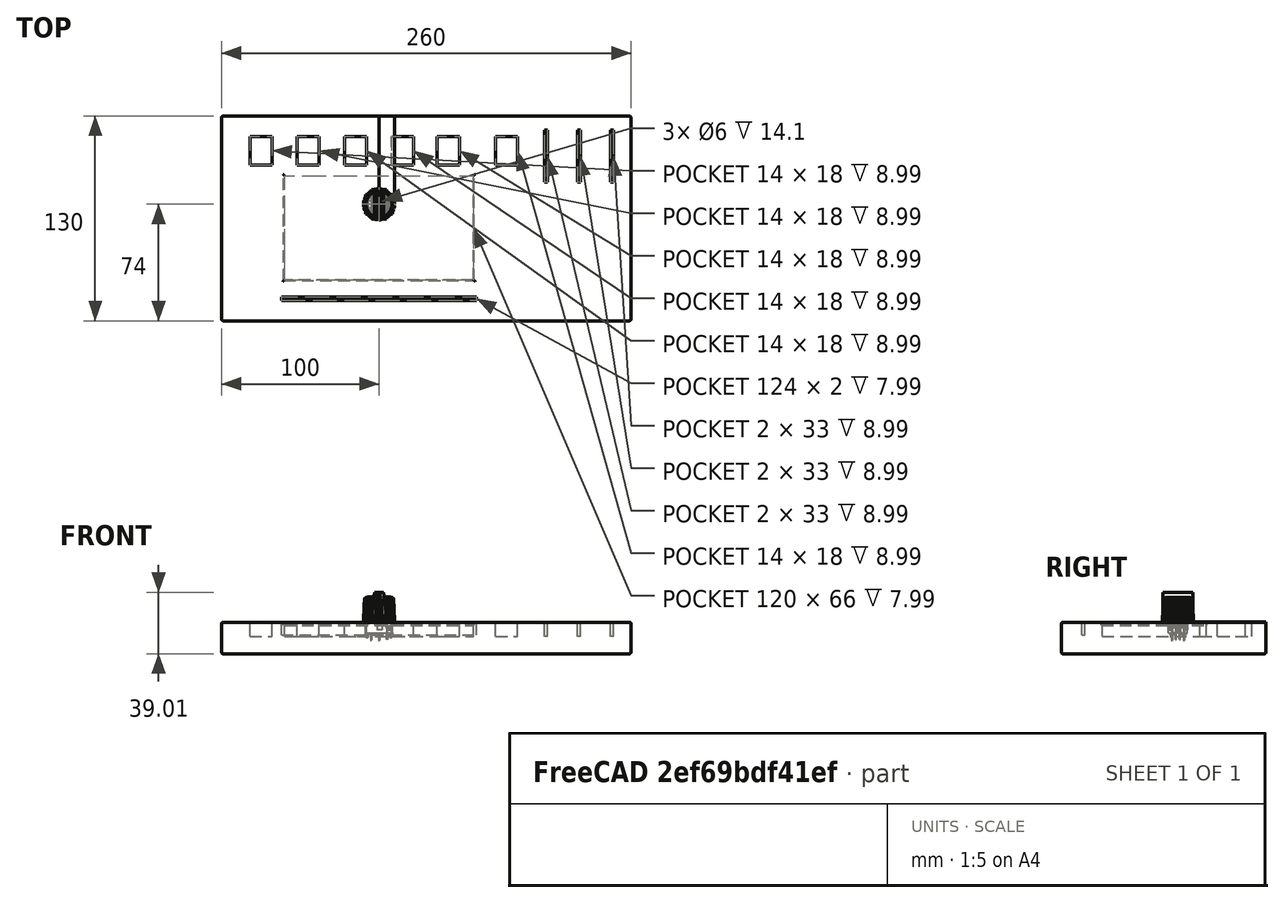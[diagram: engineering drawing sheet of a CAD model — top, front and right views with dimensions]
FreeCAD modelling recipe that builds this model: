
FCSTD DOCUMENT  (FreeCAD 0.18R14220 (Git))
Label: draw-toy
License: All rights reserved
LicenseURL: http://en.wikipedia.org/wiki/All_rights_reserved
objects: Part::Feature×42, Part::Box×33, App::DocumentObjectGroupPython×28, App::Part×20, Part::Cone×3, Part::Fillet×2, Part::Cut×2, Part::MultiFuse×1
note: 83 computed .brp shape members not serialized (recipe doc carries the construction recipe); baked Part::Feature solids carry a one-line shape summary decoded from their .brp

FEATURE [Part::Feature] Pocket004001  label="CrossfaderTop001"
  Placement = pos=(0,0,0) rot=(1,0,0;1.5708rad)
  shape: bbox 9.6 x 19 x 15 mm, 18 faces (baked)
FEATURE [Part::Feature] Pad001001  label="CrossfaderNeck001"
  Placement = pos=(0,0,0) rot=(1,0,0;1.5708rad)
  shape: bbox 6 x 1.2 x 12 mm, 12 faces (baked)
FEATURE [Part::Feature] Pocket004039  label="CrossfaderTop002"
  Placement = pos=(0,0,0) rot=(1,0,0;1.5708rad)
  shape: bbox 9.6 x 19 x 15 mm, 18 faces (baked)
FEATURE [Part::Feature] Pad001011  label="CrossfaderNeck002"
  Placement = pos=(0,0,0) rot=(1,0,0;1.5708rad)
  shape: bbox 6 x 1.2 x 12 mm, 12 faces (baked)
FEATURE [Part::Feature] Pad001012  label="CrossfaderNeck003"
  Placement = pos=(0,0,0) rot=(1,0,0;1.5708rad)
  shape: bbox 6 x 1.2 x 12 mm, 12 faces (baked)
FEATURE [Part::Feature] Pocket004040  label="CrossfaderTop003"
  Placement = pos=(0,0,0) rot=(1,0,0;1.5708rad)
  shape: bbox 9.6 x 19 x 15 mm, 18 faces (baked)
FEATURE [Part::Feature] Pad001013  label="CrossfaderNeck004"
  Placement = pos=(0,0,0) rot=(1,0,0;1.5708rad)
  shape: bbox 6 x 1.2 x 12 mm, 12 faces (baked)
FEATURE [Part::Feature] Pocket004041  label="CrossfaderTop004"
  Placement = pos=(0,0,0) rot=(1,0,0;1.5708rad)
  shape: bbox 9.6 x 19 x 15 mm, 18 faces (baked)
FEATURE [Part::Box] Box  label="Cube"
  AttacherType = Attacher::AttachEngine3D
  Height = 20
  Length = 260
  Placement = pos=(-100,-74,-20.01) rot=(0,0,1;0rad)
  Width = 130
FEATURE [Part::Fillet] Fillet004
  Base = -> Box
  Edges = 12 edges r=1: [Edge1,Edge2,Edge3,Edge4,Edge5,Edge6,Edge7,Edge8,Edge9,Edge10,Edge11,Edge12]
FEATURE [Part::Box] Box001  label="CF-Eraser-Hole"
  AttacherType = Attacher::AttachEngine3D
  Height = 10
  Length = 124
  Placement = pos=(-62,-61,-8) rot=(0,0,1;0rad)
  Width = 2
FEATURE [Part::Box] Box002  label="Btn4-Hole"
  AttacherType = Attacher::AttachEngine3D
  Height = 10
  Length = 14
  Placement = pos=(8,25,-9) rot=(0,0,1;0rad)
  Width = 18
FEATURE [Part::Box] Box003  label="Btn3-Hole"
  AttacherType = Attacher::AttachEngine3D
  Height = 10
  Length = 14
  Placement = pos=(-22,25,-9) rot=(0,0,1;0rad)
  Width = 18
FEATURE [Part::Box] Box004  label="Btn2-Hole"
  AttacherType = Attacher::AttachEngine3D
  Height = 10
  Length = 14
  Placement = pos=(-52,25,-9) rot=(0,0,1;0rad)
  Width = 18
FEATURE [Part::Box] Box005  label="Btn1-Hole"
  AttacherType = Attacher::AttachEngine3D
  Height = 10
  Length = 14
  Placement = pos=(-82,25,-9) rot=(0,0,1;0rad)
  Width = 18
FEATURE [Part::Box] Box006  label="CF-Red-Hole"
  AttacherType = Attacher::AttachEngine3D
  Height = 10
  Length = 33
  Placement = pos=(107,14,-9) rot=(0,0,1;1.5708rad)
  Width = 2
FEATURE [Part::Box] Box009  label="CF-Green-Hole"
  AttacherType = Attacher::AttachEngine3D
  Height = 10
  Length = 33
  Placement = pos=(128,14,-9) rot=(0,0,1;1.5708rad)
  Width = 2
FEATURE [Part::Box] Box010  label="CF-Blue-Hole"
  AttacherType = Attacher::AttachEngine3D
  Height = 10
  Length = 33
  Placement = pos=(149,14,-9) rot=(0,0,1;1.5708rad)
  Width = 2
FEATURE [Part::Feature] Pocket001  label="Knob002"
  Placement = pos=(0,0,0) rot=(0,0,-1;4.99164rad)
  shape: bbox 19.76 x 19.76 x 16.1 mm, 124 faces (baked)
FEATURE [Part::Feature] Pocket004042  label="Knob003"
  Placement = pos=(0,0,0) rot=(0,0,-1;2.61799rad)
  shape: bbox 19.73 x 19.73 x 16.1 mm, 124 faces (baked)
FEATURE [Part::Feature] Pocket004043  label="Knob004"
  Placement = pos=(0,0,0) rot=(0,0,-1;0.349066rad)
  shape: bbox 19.8 x 19.8 x 16.1 mm, 124 faces (baked)
FEATURE [Part::Feature] Pocket004044  label="Rot4"
  Placement = pos=(0,0,0) rot=(0,0,-1;5.41052rad)
  shape: bbox 19.8 x 19.8 x 16.1 mm, 124 faces (baked)
FEATURE [Part::Feature] Compound002  label="DigitastPins001"
  shape: bbox 16.24 x 8.62 x 4.5 mm, 46 faces, 8 solids (baked)
FEATURE [Part::Feature] Pocket006001  label="DigitastBase001"
  shape: bbox 17.3 x 12.3 x 7.9 mm, 98 faces (baked)
FEATURE [Part::Feature] Revolution001  label="ObjMode1Led"
  Placement = pos=(5.12923,-0.028118,-0.1) rot=(0.57735,0.57735,0.57735;2.0944rad)
  shape: bbox 3.4 x 3.4 x 4.5 mm, 5 faces (baked)
FEATURE [Part::Feature] Cylinder001
  Placement = pos=(7,-5,-3) rot=(-1,0,0;1.5708rad)
  shape: bbox 0.8 x 10 x 0.8 mm, 3 faces (baked)
FEATURE [Part::Feature] Pocket010001  label="DigitastTop001"
  Placement = pos=(0,0,0) rot=(1,0,0;1.5708rad)
  shape: bbox 17.1 x 12.3 x 10.94 mm, 34 faces (baked)
FEATURE [Part::Feature] Compound003  label="DigitastPins002"
  shape: bbox 16.24 x 8.62 x 4.5 mm, 46 faces, 8 solids (baked)
FEATURE [Part::Feature] Pocket010002  label="DigitastBase002"
  shape: bbox 17.3 x 12.3 x 7.9 mm, 98 faces (baked)
FEATURE [Part::Feature] Cylinder002
  Placement = pos=(7,-5,-3) rot=(-1,0,0;1.5708rad)
  shape: bbox 0.8 x 10 x 0.8 mm, 3 faces (baked)
FEATURE [Part::Feature] Revolution002  label="ObjMode2Led"
  Placement = pos=(5.12923,-0.028118,-0.1) rot=(0.57735,0.57735,0.57735;2.0944rad)
  shape: bbox 3.4 x 3.4 x 4.5 mm, 5 faces (baked)
FEATURE [Part::Feature] Pocket010003  label="DigitastTop002"
  Placement = pos=(0,0,0) rot=(1,0,0;1.5708rad)
  shape: bbox 17.1 x 12.3 x 10.94 mm, 34 faces (baked)
FEATURE [Part::Feature] Compound004  label="DigitastPins003"
  shape: bbox 16.24 x 8.62 x 4.5 mm, 46 faces, 8 solids (baked)
FEATURE [Part::Feature] Pocket010004  label="DigitastBase003"
  shape: bbox 17.3 x 12.3 x 7.9 mm, 98 faces (baked)
FEATURE [Part::Feature] Cylinder003
  Placement = pos=(7,-5,-3) rot=(-1,0,0;1.5708rad)
  shape: bbox 0.8 x 10 x 0.8 mm, 3 faces (baked)
FEATURE [Part::Feature] Revolution003  label="ObjMode3Led"
  Placement = pos=(5.12923,-0.028118,-0.1) rot=(0.57735,0.57735,0.57735;2.0944rad)
  shape: bbox 3.4 x 3.4 x 4.5 mm, 5 faces (baked)
FEATURE [Part::Feature] Pocket010005  label="DigitastTop003"
  Placement = pos=(0,0,0) rot=(1,0,0;1.5708rad)
  shape: bbox 17.1 x 12.3 x 10.94 mm, 34 faces (baked)
FEATURE [Part::Feature] Compound005  label="DigitastPins004"
  shape: bbox 16.24 x 8.62 x 4.5 mm, 46 faces, 8 solids (baked)
FEATURE [Part::Feature] Pocket010006  label="DigitastBase004"
  shape: bbox 17.3 x 12.3 x 7.9 mm, 98 faces (baked)
FEATURE [Part::Feature] Cylinder004
  Placement = pos=(7,-5,-3) rot=(-1,0,0;1.5708rad)
  shape: bbox 0.8 x 10 x 0.8 mm, 3 faces (baked)
FEATURE [Part::Feature] Revolution004  label="ObjMode4Led"
  Placement = pos=(5.12923,-0.028118,-0.1) rot=(0.57735,0.57735,0.57735;2.0944rad)
  shape: bbox 3.4 x 3.4 x 4.5 mm, 5 faces (baked)
FEATURE [Part::Feature] Pocket010007  label="DigitastTop004"
  Placement = pos=(0,0,0) rot=(1,0,0;1.5708rad)
  shape: bbox 17.1 x 12.3 x 10.94 mm, 34 faces (baked)
FEATURE [Part::Box] Box011  label="DisplayBackground"
  AttacherType = Attacher::AttachEngine3D
  Height = 1
  Length = 121
  Placement = pos=(-60.5,-48.5,-2) rot=(0,0,1;0rad)
  Width = 67
FEATURE [Part::Box] Box012  label="Cube002"
  AttacherType = Attacher::AttachEngine3D
  Height = 0.01
  Length = 121
  Placement = pos=(-60.5,-48.5,-1) rot=(0,0,1;0rad)
  Width = 67
FEATURE [App::DocumentObjectGroupPython] FPSimDisplay  # scripted group (container) (typed FeaturePython)
  Group = -> [Box012]
  ResolutionX = 300
  ResolutionY = 200
FEATURE [Part::Box] Box013  label="Cube003"
  AttacherType = Attacher::AttachEngine3D
  Height = 10
  Length = 120
  Placement = pos=(-60,-48,-9) rot=(0,0,1;0rad)
  Width = 66
FEATURE [App::DocumentObjectGroupPython] FPSimButton  label="Mode1Btn"  # scripted group (container) (typed FeaturePython)
  Group = -> [Pocket010001,Cylinder001]
  RotationAngle = -6
  RotationAxis = (0,1,0)
  RotationCenter = (7,5,-3)
  SwitchMode = false
  Translation = (0.3,0,0)
FEATURE [App::DocumentObjectGroupPython] FPSimButton001  label="Mode2Btn"  # scripted group (container) (typed FeaturePython)
  Group = -> [Pocket010003,Cylinder002]
  RotationAngle = -6
  RotationAxis = (0,1,0)
  RotationCenter = (7,5,-3)
  SwitchMode = false
  Translation = (0.3,0,0)
FEATURE [App::DocumentObjectGroupPython] FPSimButton002  label="Mode3Btn"  # scripted group (container) (typed FeaturePython)
  Group = -> [Pocket010005,Cylinder003]
  RotationAngle = -6
  RotationAxis = (0,1,0)
  RotationCenter = (7,5,-3)
  SwitchMode = false
  Translation = (0.3,0,0)
FEATURE [App::DocumentObjectGroupPython] FPSimButton003  label="Mode4Btn"  # scripted group (container) (typed FeaturePython)
  Group = -> [Pocket010007,Cylinder004]
  RotationAngle = -6
  RotationAxis = (0,1,0)
  RotationCenter = (7,5,-3)
  SwitchMode = false
  Translation = (0.3,0,0)
FEATURE [Part::Box] Box014  label="Cube004"
  AttacherType = Attacher::AttachEngine3D
  Height = 0.01
  Length = 121
  Placement = pos=(-60.5,-48.5,-0.9) rot=(0,0,1;0rad)
  Width = 67
FEATURE [Part::Feature] Compound006  label="DigitastPins005"
  shape: bbox 16.24 x 8.62 x 4.5 mm, 46 faces, 8 solids (baked)
FEATURE [Part::Feature] Pocket010008  label="DigitastBase005"
  shape: bbox 17.3 x 12.3 x 7.9 mm, 98 faces (baked)
FEATURE [Part::Feature] Revolution005  label="ObjColorModLed"
  Placement = pos=(5.12923,-0.028118,-0.1) rot=(0.57735,0.57735,0.57735;2.0944rad)
  shape: bbox 3.4 x 3.4 x 4.5 mm, 5 faces (baked)
FEATURE [Part::Feature] Cylinder005
  Placement = pos=(7,-5,-3) rot=(-1,0,0;1.5708rad)
  shape: bbox 0.8 x 10 x 0.8 mm, 3 faces (baked)
FEATURE [Part::Feature] Pocket010009  label="DigitastTop005"
  Placement = pos=(0,0,0) rot=(1,0,0;1.5708rad)
  shape: bbox 17.1 x 12.3 x 10.94 mm, 34 faces (baked)
FEATURE [App::DocumentObjectGroupPython] FPSimButton004  label="ColorAutomationBtn"  # scripted group (container) (typed FeaturePython)
  Group = -> [Pocket010009,Cylinder005]
  RotationAngle = -6
  RotationAxis = (0,1,0)
  RotationCenter = (7,5,-3)
  SwitchMode = false
  Translation = (0.3,0,0)
FEATURE [Part::Box] Box015  label="ModBtnHole"
  AttacherType = Attacher::AttachEngine3D
  Height = 10
  Length = 14
  Placement = pos=(74,25,-9) rot=(0,0,1;0rad)
  Width = 18
FEATURE [App::DocumentObjectGroupPython] FPSimRotaryEncoder  label="X_POS1"  # scripted group (container) (typed FeaturePython)
  Group = -> [Pocket001]
  IncrementsPerRev = 64
  MouseSensitivity = 1
  NumSnapInPositions = 0
  PushButton = false
  PushButtonDepth = 1
  RotationAxis = (0,0,-1)
  RotationCenter = (0,0,0)
FEATURE [App::Part] Part  label="Rot001"
  Group = -> [Pocket001,FPSimRotaryEncoder]
  License = CC BY 3.0
  LicenseURL = http://creativecommons.org/licenses/by/3.0/
  Origin = -> Origin
  Placement = pos=(-79,0,1) rot=(0,0,1;0rad)
FEATURE [App::DocumentObjectGroupPython] FPSimRotaryEncoder001  label="Y_POS1"  # scripted group (container) (typed FeaturePython)
  Group = -> [Pocket004042]
  IncrementsPerRev = 64
  MouseSensitivity = 1
  NumSnapInPositions = 0
  PushButton = false
  PushButtonDepth = 1
  RotationAxis = (0,0,-1)
  RotationCenter = (0,0,0)
FEATURE [App::Part] Part012  label="Rot002"
  Group = -> [Pocket004042,FPSimRotaryEncoder001]
  License = CC BY 3.0
  LicenseURL = http://creativecommons.org/licenses/by/3.0/
  Origin = -> Origin013
  Placement = pos=(-79,-37,1) rot=(0,0,1;0rad)
FEATURE [App::DocumentObjectGroupPython] FPSimRotaryEncoder002  label="X_POS2"  # scripted group (container) (typed FeaturePython)
  Group = -> [Pocket004043]
  IncrementsPerRev = 64
  MouseSensitivity = 1
  NumSnapInPositions = 0
  PushButton = false
  PushButtonDepth = 1
  RotationAxis = (0,0,-1)
  RotationCenter = (0,0,0)
FEATURE [App::Part] Part014  label="Rot004"
  Group = -> [Pocket004043,FPSimRotaryEncoder002]
  License = CC BY 3.0
  LicenseURL = http://creativecommons.org/licenses/by/3.0/
  Origin = -> Origin015
  Placement = pos=(80,0,1) rot=(0,0,1;0rad)
FEATURE [App::DocumentObjectGroupPython] FPSimRotaryEncoder003  label="Y_POS2"  # scripted group (container) (typed FeaturePython)
  Group = -> [Pocket004044]
  IncrementsPerRev = 64
  MouseSensitivity = 1
  NumSnapInPositions = 0
  PushButton = false
  PushButtonDepth = 1
  RotationAxis = (0,0,-1)
  RotationCenter = (0,0,0)
FEATURE [App::Part] Part013  label="Rot003"
  Group = -> [Pocket004044,FPSimRotaryEncoder003]
  License = CC BY 3.0
  LicenseURL = http://creativecommons.org/licenses/by/3.0/
  Origin = -> Origin014
  Placement = pos=(80,-37,1) rot=(0,0,1;0rad)
FEATURE [Part::Cone] Cone
  Angle = 360
  AttacherType = Attacher::AttachEngine3D
  Height = 10
  Placement = pos=(0,0,10) rot=(1,0,0;3.14159rad)
  Radius1 = 4
  Radius2 = 5
FEATURE [Part::Box] Box016  label="Cube005"
  AttacherType = Attacher::AttachEngine3D
  Height = 10
  Length = 1
  Placement = pos=(-0.5,0,0) rot=(0,0,1;0rad)
  Width = 5
FEATURE [Part::Cone] Cone001
  Angle = 360
  AttacherType = Attacher::AttachEngine3D
  Height = 10
  Placement = pos=(0,0,10) rot=(1,0,0;3.14159rad)
  Radius1 = 4
  Radius2 = 5
FEATURE [Part::Box] Box017  label="Cube006"
  AttacherType = Attacher::AttachEngine3D
  Height = 10
  Length = 1
  Placement = pos=(-0.5,0,0) rot=(0,0,1;0rad)
  Width = 5
FEATURE [Part::Cone] Cone002
  Angle = 360
  AttacherType = Attacher::AttachEngine3D
  Height = 10
  Placement = pos=(0,0,10) rot=(1,0,0;3.14159rad)
  Radius1 = 4
  Radius2 = 5
FEATURE [Part::Box] Box018  label="Cube007"
  AttacherType = Attacher::AttachEngine3D
  Height = 10
  Length = 1
  Placement = pos=(-0.5,0,0) rot=(0,0,1;0rad)
  Width = 5
FEATURE [App::DocumentObjectGroupPython] FPSimRotaryPotentiometer  label="PotFreqRed"  # scripted group (container) (typed FeaturePython)
  Group = -> [Box016,Cone]
  IncrementsOnWholeArc = 64
  MouseSensitivity = 1
  NegativeRotLimitDeg = 120
  NumSnapInPositions = 0
  PositiveRotLimitDeg = 120
  RotationAxis = (0,0,-1)
  RotationCenter = (0,0,0)
FEATURE [App::Part] Part020  label="PartFreqRed"
  Group = -> [Cone,Box016,FPSimRotaryPotentiometer]
  License = CC BY 3.0
  LicenseURL = http://creativecommons.org/licenses/by/3.0/
  Origin = -> Origin021
  Placement = pos=(106,0,0) rot=(0,0,1;0rad)
FEATURE [App::DocumentObjectGroupPython] FPSimRotaryPotentiometer001  label="PotFreqGreen"  # scripted group (container) (typed FeaturePython)
  Group = -> [Box017,Cone001]
  IncrementsOnWholeArc = 64
  MouseSensitivity = 1
  NegativeRotLimitDeg = 120
  NumSnapInPositions = 0
  PositiveRotLimitDeg = 120
  RotationAxis = (0,0,-1)
  RotationCenter = (0,0,0)
FEATURE [App::Part] Part021  label="PartFreqGreen"
  Group = -> [Cone001,Box017,FPSimRotaryPotentiometer001]
  License = CC BY 3.0
  LicenseURL = http://creativecommons.org/licenses/by/3.0/
  Origin = -> Origin022
  Placement = pos=(127,0,0) rot=(0,0,1;0rad)
FEATURE [App::DocumentObjectGroupPython] FPSimRotaryPotentiometer002  label="PotFreqBlue"  # scripted group (container) (typed FeaturePython)
  Group = -> [Box018,Cone002]
  IncrementsOnWholeArc = 64
  MouseSensitivity = 1
  NegativeRotLimitDeg = 120
  NumSnapInPositions = 0
  PositiveRotLimitDeg = 120
  RotationAxis = (0,0,-1)
  RotationCenter = (0,0,0)
FEATURE [App::Part] Part022  label="PartFreqBlue"
  Group = -> [Cone002,Box018,FPSimRotaryPotentiometer002]
  License = CC BY 3.0
  LicenseURL = http://creativecommons.org/licenses/by/3.0/
  Origin = -> Origin023
  Placement = pos=(148,0,0) rot=(0,0,1;0rad)
FEATURE [Part::Box] Box019  label="ObjAmpRedTouch"
  AttacherType = Attacher::AttachEngine3D
  Height = 0.1
  Length = 10
  Width = 56
FEATURE [App::DocumentObjectGroupPython] FPSimTouchSurface001  label="AmpRedTouch"  # scripted group (container) (typed FeaturePython)
  Group = -> [Box019]
  ResolutionX = 100
  ResolutionY = 10
FEATURE [App::Part] Part023  label="PartAmpRedTouch"
  Group = -> [Box019,FPSimTouchSurface001]
  License = CC BY 3.0
  LicenseURL = http://creativecommons.org/licenses/by/3.0/
  Origin = -> Origin024
  Placement = pos=(101,-67,0) rot=(0,0,1;0rad)
FEATURE [Part::Box] Box020  label="ObjAmpGreenTouch"
  AttacherType = Attacher::AttachEngine3D
  Height = 0.1
  Length = 10
  Width = 56
FEATURE [App::DocumentObjectGroupPython] FPSimTouchSurface002  label="AmpGreenTouch"  # scripted group (container) (typed FeaturePython)
  Group = -> [Box020]
  ResolutionX = 100
  ResolutionY = 10
FEATURE [App::Part] Part024  label="PartAmpGreenTouch"
  Group = -> [Box020,FPSimTouchSurface002]
  License = CC BY 3.0
  LicenseURL = http://creativecommons.org/licenses/by/3.0/
  Origin = -> Origin025
  Placement = pos=(122,-67,0) rot=(0,0,1;0rad)
FEATURE [Part::Box] Box021  label="ObjAmpBlueTouch"
  AttacherType = Attacher::AttachEngine3D
  Height = 0.1
  Length = 10
  Width = 56
FEATURE [App::DocumentObjectGroupPython] FPSimTouchSurface003  label="AmpBlueTouch"  # scripted group (container) (typed FeaturePython)
  Group = -> [Box021]
  ResolutionX = 100
  ResolutionY = 10
FEATURE [App::Part] Part025  label="PartAmpBlueTouch"
  Group = -> [Box021,FPSimTouchSurface003]
  License = CC BY 3.0
  LicenseURL = http://creativecommons.org/licenses/by/3.0/
  Origin = -> Origin026
  Placement = pos=(143,-67,0) rot=(0,0,1;0rad)
FEATURE [Part::Feature] Compound007  label="DigitastPins006"
  shape: bbox 16.24 x 8.62 x 4.5 mm, 46 faces, 8 solids (baked)
FEATURE [Part::Feature] Pocket010010  label="DigitastBase006"
  shape: bbox 17.3 x 12.3 x 7.9 mm, 98 faces (baked)
FEATURE [Part::Feature] Cylinder006
  Placement = pos=(7,-5,-3) rot=(-1,0,0;1.5708rad)
  shape: bbox 0.8 x 10 x 0.8 mm, 3 faces (baked)
FEATURE [Part::Feature] Revolution006  label="ObjMode5Led"
  Placement = pos=(5.12923,-0.028118,-0.1) rot=(0.57735,0.57735,0.57735;2.0944rad)
  shape: bbox 3.4 x 3.4 x 4.5 mm, 5 faces (baked)
FEATURE [Part::Feature] Pocket010011  label="DigitastTop006"
  Placement = pos=(0,0,0) rot=(1,0,0;1.5708rad)
  shape: bbox 17.1 x 12.3 x 10.94 mm, 34 faces (baked)
FEATURE [App::DocumentObjectGroupPython] FPSimButton005  label="Mode5Btn"  # scripted group (container) (typed FeaturePython)
  Group = -> [Pocket010011,Cylinder006]
  RotationAngle = -6
  RotationAxis = (0,1,0)
  RotationCenter = (7,5,-3)
  SwitchMode = false
  Translation = (0.3,0,0)
FEATURE [Part::Box] Box022  label="Btn5-Hole"
  AttacherType = Attacher::AttachEngine3D
  Height = 10
  Length = 14
  Placement = pos=(37,25,-9) rot=(0,0,1;0rad)
  Width = 18
FEATURE [Part::MultiFuse] Fusion  label="Holes"
  Shapes = -> [Box001,Box002,Box003,Box004,Box005,Box006,Box009,Box010,Box015,Box022]
FEATURE [Part::Cut] Cut016  label="Panel"
  Base = -> Fillet004
  Tool = -> Fusion
FEATURE [Part::Cut] Cut
  Base = -> Cut016
  Tool = -> Box013
FEATURE [Part::Fillet] Fillet  label="Box"
  Base = -> Cut
  Edges = 4 edges r=1: [Edge56,Edge57,Edge58,Edge59]
FEATURE [Part::Box] Box023  label="Cube008"
  AttacherType = Attacher::AttachEngine3D
  Height = 0.1
  Length = 1.6
  Placement = pos=(-0.8,-9.4,18.7) rot=(0,0,1;0rad)
  Width = 18.8
FEATURE [Part::Box] Box024  label="Cube009"
  AttacherType = Attacher::AttachEngine3D
  Height = 0.1
  Length = 1.6
  Placement = pos=(-0.8,-9.4,18.7) rot=(1,0,0;4.71239rad)
  Width = 14.8
FEATURE [Part::Box] Box025  label="Cube010"
  AttacherType = Attacher::AttachEngine3D
  Height = 0.1
  Length = 1.6
  Placement = pos=(-0.8,9.35,18.7) rot=(-1,0,0;1.5708rad)
  Width = 14.8
FEATURE [App::DocumentObjectGroupPython] FPSimLinearPotentiometer  label="PotEraser"  # scripted group (container) (typed FeaturePython)
  Group = -> [Pocket004001,Pad001001,Box025,Box024,Box023]
  NegativeDistLimit = 59
  NumSnapInPositions = 0
  PositiveDirection = (1,0,0)
  PositiveDistLimit = 59
  Resolution = 1024
FEATURE [App::Part] Part004  label="CF-Eraser"
  Group = -> [Pocket004001,Pad001001,FPSimLinearPotentiometer,Box025,Box024,Box023]
  License = CC BY 3.0
  LicenseURL = http://creativecommons.org/licenses/by/3.0/
  Origin = -> Origin005
  Placement = pos=(0,-60,0) rot=(0,0,1;0rad)
FEATURE [Part::Box] Box026  label="Cube011"
  AttacherType = Attacher::AttachEngine3D
  Height = 0.1
  Length = 1.6
  Placement = pos=(-0.8,9.35,18.7) rot=(-1,0,0;1.5708rad)
  Width = 14.8
FEATURE [Part::Box] Box027  label="Cube012"
  AttacherType = Attacher::AttachEngine3D
  Height = 0.1
  Length = 1.6
  Placement = pos=(-0.8,-9.4,18.7) rot=(-1,0,0;1.5708rad)
  Width = 14.8
FEATURE [Part::Box] Box028  label="Cube013"
  AttacherType = Attacher::AttachEngine3D
  Height = 0.1
  Length = 1.6
  Placement = pos=(-0.8,-9.4,18.7) rot=(0,0,1;0rad)
  Width = 18.8
FEATURE [App::DocumentObjectGroupPython] FPSimLinearPotentiometer004  label="PotRed"  # scripted group (container) (typed FeaturePython)
  Group = -> [Pocket004039,Pad001011,Box028,Box027,Box026]
  NegativeDistLimit = 13
  NumSnapInPositions = 0
  PositiveDirection = (-1,0,0)
  PositiveDistLimit = 13
  Resolution = 255
FEATURE [App::Part] Part009  label="CF-Red"
  Group = -> [Pocket004039,Pad001011,FPSimLinearPotentiometer004,Box028,Box027,Box026]
  License = CC BY 3.0
  LicenseURL = http://creativecommons.org/licenses/by/3.0/
  Origin = -> Origin010
  Placement = pos=(106,30,0) rot=(0,0,1;4.71239rad)
FEATURE [Part::Box] Box029  label="Cube014"
  AttacherType = Attacher::AttachEngine3D
  Height = 0.1
  Length = 1.6
  Placement = pos=(-0.8,9.35,18.7) rot=(-1,0,0;1.5708rad)
  Width = 14.8
FEATURE [Part::Box] Box030  label="Cube015"
  AttacherType = Attacher::AttachEngine3D
  Height = 0.1
  Length = 1.6
  Placement = pos=(-0.8,-9.4,18.7) rot=(-1,0,0;1.5708rad)
  Width = 14.8
FEATURE [Part::Box] Box031  label="Cube016"
  AttacherType = Attacher::AttachEngine3D
  Height = 0.1
  Length = 1.6
  Placement = pos=(-0.8,-9.4,18.7) rot=(0,0,1;0rad)
  Width = 18.8
FEATURE [App::DocumentObjectGroupPython] FPSimLinearPotentiometer005  label="PotGreen"  # scripted group (container) (typed FeaturePython)
  Group = -> [Pad001012,Pocket004040,Box029,Box030,Box031]
  NegativeDistLimit = 13
  NumSnapInPositions = 0
  PositiveDirection = (-1,0,0)
  PositiveDistLimit = 13
  Resolution = 255
FEATURE [App::Part] Part010  label="CF-Green"
  Group = -> [Pad001012,Pocket004040,FPSimLinearPotentiometer005,Box029,Box030,Box031]
  License = CC BY 3.0
  LicenseURL = http://creativecommons.org/licenses/by/3.0/
  Origin = -> Origin011
  Placement = pos=(127,30,0) rot=(0,0,1;4.71239rad)
FEATURE [Part::Box] Box032  label="Cube017"
  AttacherType = Attacher::AttachEngine3D
  Height = 0.1
  Length = 1.6
  Placement = pos=(-0.8,9.35,18.7) rot=(-1,0,0;1.5708rad)
  Width = 14.8
FEATURE [Part::Box] Box033  label="Cube018"
  AttacherType = Attacher::AttachEngine3D
  Height = 0.1
  Length = 1.6
  Placement = pos=(-0.8,-9.4,18.7) rot=(-1,0,0;1.5708rad)
  Width = 14.8
FEATURE [Part::Box] Box034  label="Cube019"
  AttacherType = Attacher::AttachEngine3D
  Height = 0.1
  Length = 1.6
  Placement = pos=(-0.8,-9.4,18.7) rot=(0,0,1;0rad)
  Width = 18.8
FEATURE [App::DocumentObjectGroupPython] FPSimLinearPotentiometer006  label="PotBlue"  # scripted group (container) (typed FeaturePython)
  Group = -> [Pocket004041,Pad001013,Box032,Box033,Box034]
  NegativeDistLimit = 13
  NumSnapInPositions = 0
  PositiveDirection = (-1,0,0)
  PositiveDistLimit = 13
  Resolution = 255
FEATURE [App::Part] Part011  label="CF-Blue"
  Group = -> [Pad001013,Pocket004041,FPSimLinearPotentiometer006,Box032,Box033,Box034]
  License = CC BY 3.0
  LicenseURL = http://creativecommons.org/licenses/by/3.0/
  Origin = -> Origin012
  Placement = pos=(148,30,0) rot=(0,0,1;4.71239rad)
FEATURE [App::DocumentObjectGroupPython] FPSimTouchSurface  label="TouchSurface"  # scripted group (container) (typed FeaturePython)
  Group = -> [Box014]
  ResolutionX = 300
  ResolutionY = 200
FEATURE [App::DocumentObjectGroupPython] FPSimLED  label="Mode1Led"  # scripted group (container) (typed FeaturePython)
  Group = -> [Revolution001]
FEATURE [App::Part] Part015  label="Btn001"
  Group = -> [Compound002,Pocket006001,Cylinder001,Pocket010001,FPSimButton,Revolution001,FPSimLED]
  License = CC BY 3.0
  LicenseURL = http://creativecommons.org/licenses/by/3.0/
  Origin = -> Origin016
  Placement = pos=(-75,34,-2) rot=(0,0,1;1.5708rad)
FEATURE [App::DocumentObjectGroupPython] FPSimLED001  label="Mode2Led"  # scripted group (container) (typed FeaturePython)
  Group = -> [Revolution002]
FEATURE [App::Part] Part016  label="Btn002"
  Group = -> [Compound003,Pocket010002,Cylinder002,Pocket010003,FPSimButton001,Revolution002,FPSimLED001]
  License = CC BY 3.0
  LicenseURL = http://creativecommons.org/licenses/by/3.0/
  Origin = -> Origin017
  Placement = pos=(-45,34,-2) rot=(0,0,1;1.5708rad)
FEATURE [App::DocumentObjectGroupPython] FPSimLED002  label="Mode3Led"  # scripted group (container) (typed FeaturePython)
  Group = -> [Revolution003]
FEATURE [App::Part] Part017  label="Btn003"
  Group = -> [Compound004,Pocket010004,Cylinder003,Pocket010005,FPSimButton002,Revolution003,FPSimLED002]
  License = CC BY 3.0
  LicenseURL = http://creativecommons.org/licenses/by/3.0/
  Origin = -> Origin018
  Placement = pos=(-15,34,-2) rot=(0,0,1;1.5708rad)
FEATURE [App::DocumentObjectGroupPython] FPSimLED003  label="Mode4Led"  # scripted group (container) (typed FeaturePython)
  Group = -> [Revolution004]
FEATURE [App::Part] Part018  label="Btn004"
  Group = -> [Compound005,Pocket010006,Cylinder004,Pocket010007,FPSimButton003,Revolution004,FPSimLED003]
  License = CC BY 3.0
  LicenseURL = http://creativecommons.org/licenses/by/3.0/
  Origin = -> Origin019
  Placement = pos=(15,34,-2) rot=(0,0,1;1.5708rad)
FEATURE [App::DocumentObjectGroupPython] FPSimLED004  label="Mode5Led"  # scripted group (container) (typed FeaturePython)
  Group = -> [Revolution006]
FEATURE [App::Part] Part026  label="Btn005"
  Group = -> [Compound007,Pocket010010,Cylinder006,Pocket010011,FPSimButton005,Revolution006,FPSimLED004]
  License = CC BY 3.0
  LicenseURL = http://creativecommons.org/licenses/by/3.0/
  Origin = -> Origin027
  Placement = pos=(44,34,-2) rot=(0,0,1;1.5708rad)
FEATURE [App::DocumentObjectGroupPython] FPSimLED005  label="ColorModLed"  # scripted group (container) (typed FeaturePython)
  Group = -> [Revolution005]
FEATURE [App::Part] Part019  label="PartColorAutomationEanbleBtn"
  Group = -> [Compound006,Pocket010008,Cylinder005,Pocket010009,FPSimButton004,Revolution005,FPSimLED005]
  License = CC BY 3.0
  LicenseURL = http://creativecommons.org/licenses/by/3.0/
  Origin = -> Origin020
  Placement = pos=(81,34,-2) rot=(0,0,1;1.5708rad)
